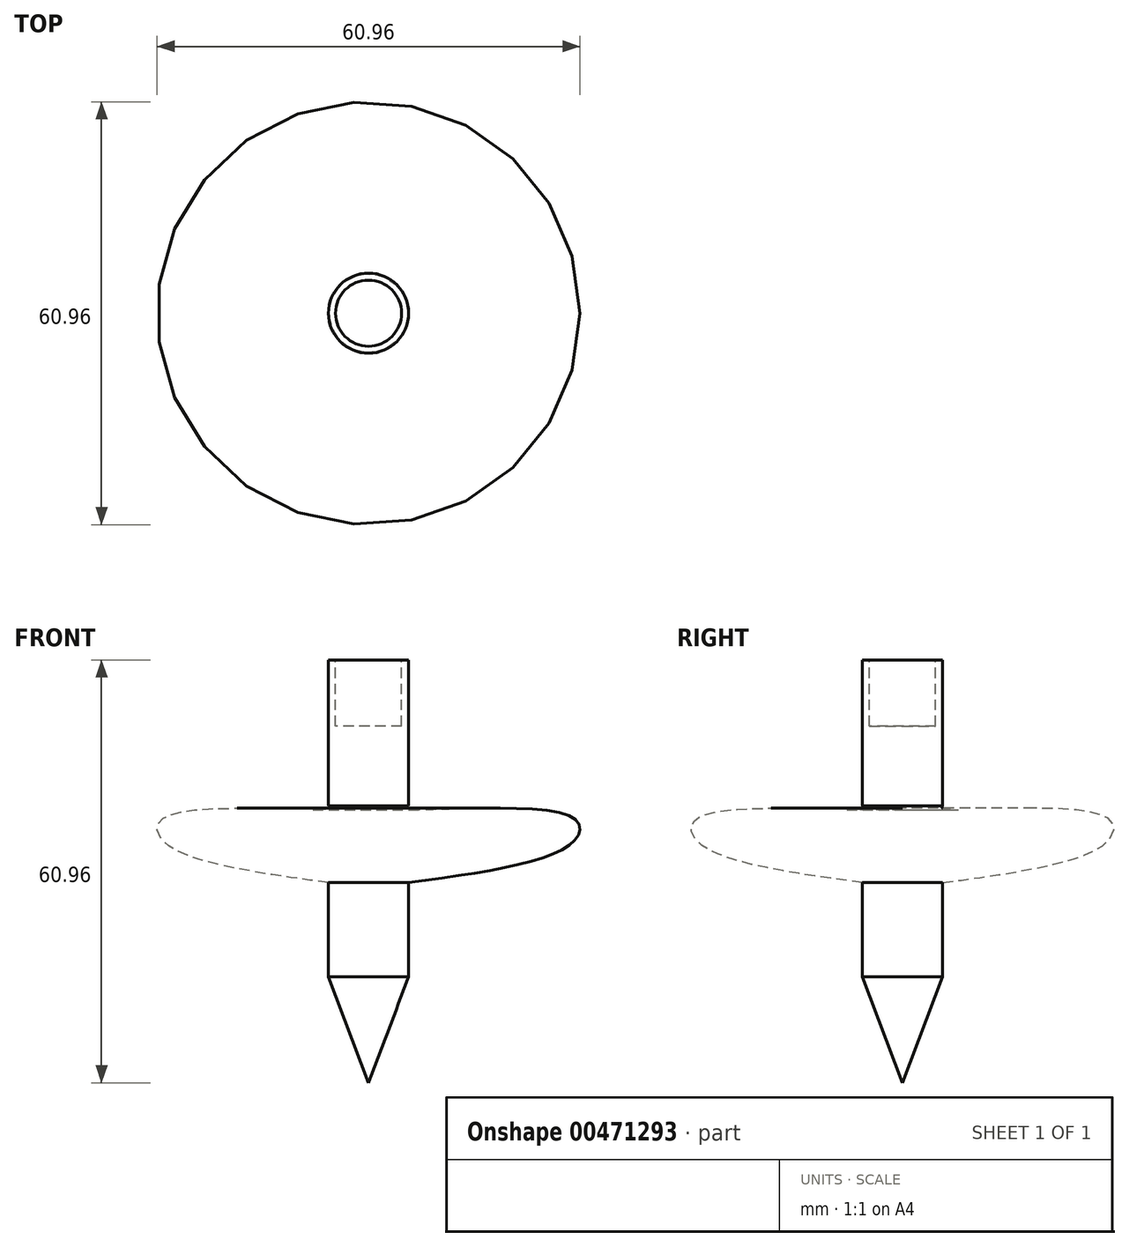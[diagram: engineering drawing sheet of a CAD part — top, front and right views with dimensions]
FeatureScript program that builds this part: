
annotation { "Feature Type Name" : "Feature", "Feature Type Description" : "" }
export const myFeature = defineFeature(function(context is Context, id is Id, definition is map)
    precondition{}
    {
        {
            var Q0;
            Q0=qCreatedBy(makeId("Front.planeOp"),FACE);
            var sketch = newSketch(context, id + "F0", { "sketchPlane" : qUnion([Q0])});
            skLineSegment(sketch, "E0", {"start": v(0, 0) * mm, "end": v(5.78, 15.28) * mm});
            skLineSegment(sketch, "E1", {"start": v(5.78, 15.28) * mm, "end": v(5.78, 28.84) * mm});
            skFitSpline(sketch, "E2", {"points": [v(5.78, 28.84) * mm, v(29.69, 34.9) * mm, v(28.97, 38.48) * mm, v(5.78, 39.55) * mm, v(5.78, 39.9) * mm], "startDerivative": vector(77.71, 10.67) * mm, "endDerivative": vector(5, 8.16) * mm});
            skLineSegment(sketch, "E3", {"start": v(5.78, 39.9) * mm, "end": v(5.78, 60.96) * mm});
            skLineSegment(sketch, "E4", {"start": v(5.78, 60.96) * mm, "end": v(0, 60.96) * mm});
            skLineSegment(sketch, "E5", {"start": v(0, 60.96) * mm, "end": v(0, 0) * mm});
            skSolve(sketch);
        }
        {
            var Q0;
            Q0=makeQuery(id+"F0.imprint","IMPRINT",FACE,{"disambiguationData":[TD([[makeQuery(id+"F0.imprint","IMPRINT",EDGE,{"derivedFrom":sQuery(id+"F0.wireOp",EDGE,"E0")}),1.0]])]});
            var Q1;
            Q1=sQuery(id+"F0.wireOp",EDGE,"E5");
            revolve(context, id + "F1", {"entities" : qUnion([Q0]), "axis" : qUnion([Q1]), "revolveType" : RevolveType.FULL});
        }
        {
            var Q0;
            Q0=makeQuery(id+"F1.opRevolve","SWEPT_FACE",FACE,{"disambiguationData":[OSD([sQuery(id+"F0.wireOp",EDGE,"E4")])]});
            var sketch = newSketch(context, id + "F2", { "sketchPlane" : qUnion([Q0])});
            skCircle(sketch, "E6", {"center": v(0, 0) * mm, "radius": 4.76 * mm});
            skSolve(sketch);
        }
        {
            var Q0;
            Q0=makeQuery(id+"F2.imprint","IMPRINT",FACE,{"disambiguationData":[TD([[makeQuery(id+"F2.imprint","IMPRINT",EDGE,{"derivedFrom":sQuery(id+"F2.wireOp",EDGE,"E6")}),1.0]])]});
            extrude(context, id + "F3", {"entities" : qUnion([Q0]), "operationType" : NewBodyOperationType.REMOVE, "depth" : -9.52 * mm});
        }
        {
            var Q0;
            Q0=makeQuery(id+"F2.imprint","IMPRINT",FACE,{"disambiguationData":[TD([[makeQuery(id+"F2.imprint","IMPRINT",EDGE,{"derivedFrom":sQuery(id+"F2.wireOp",EDGE,"E6")}),1.0]])]});
            extrude(context, id + "F4", {"entities" : qUnion([Q0]), "oppositeDirection" : true, "depth" : 9.52 * mm});
        }
    });
